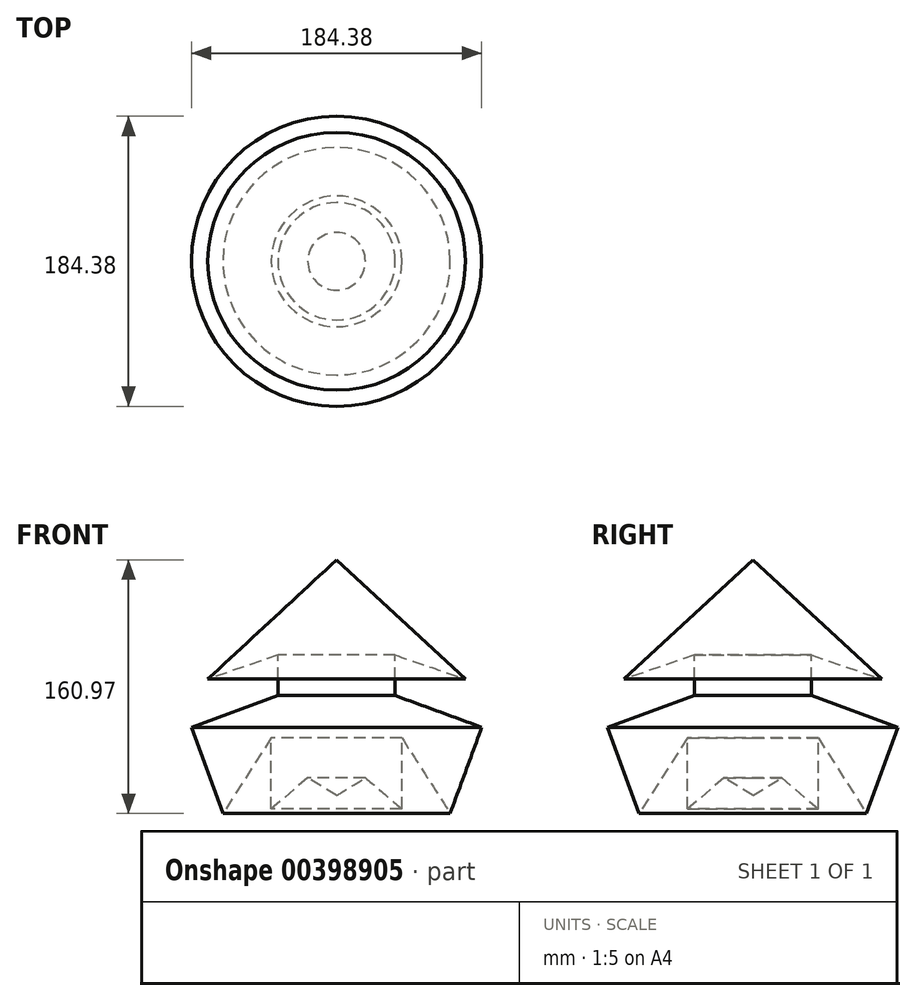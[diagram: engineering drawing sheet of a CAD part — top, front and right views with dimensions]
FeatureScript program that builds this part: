
annotation { "Feature Type Name" : "Feature", "Feature Type Description" : "" }
export const myFeature = defineFeature(function(context is Context, id is Id, definition is map)
    precondition{}
    {
        {
            var Q0;
            Q0=qCreatedBy(makeId("Right.planeOp"),FACE);
            var sketch = newSketch(context, id + "F0", { "sketchPlane" : qUnion([Q0])});
            skLineSegment(sketch, "E0", {"start": v(0, 75.7) * mm, "end": v(0, -73.9) * mm});
            skLineSegment(sketch, "E1", {"start": v(0, 75.7) * mm, "end": v(81.81, 0) * mm});
            skLineSegment(sketch, "E2", {"start": v(81.81, 0) * mm, "end": v(37.24, 15.22) * mm});
            skLineSegment(sketch, "E3", {"start": v(37.24, 15.22) * mm, "end": v(37.24, -10.5) * mm});
            skLineSegment(sketch, "E4", {"start": v(37.24, -10.5) * mm, "end": v(92.2, -30.59) * mm});
            skLineSegment(sketch, "E5", {"start": v(92.2, -30.59) * mm, "end": v(71.12, -88.2) * mm});
            skLineSegment(sketch, "E6", {"start": v(72.19, -85.28) * mm, "end": v(41.52, -37.33) * mm});
            skLineSegment(sketch, "E7", {"start": v(41.52, -37.33) * mm, "end": v(41.52, -82.44) * mm});
            skLineSegment(sketch, "E8", {"start": v(41.52, -82.44) * mm, "end": v(18.32, -62.74) * mm});
            skLineSegment(sketch, "E9", {"start": v(18.32, -62.74) * mm, "end": v(0, -73.9) * mm});
            skSolve(sketch);
        }
        {
            var Q0;
            Q0=makeQuery(id+"F0.imprint","IMPRINT",FACE,{"disambiguationData":[TD([[makeQuery(id+"F0.imprint","IMPRINT",EDGE,{"derivedFrom":sQuery(id+"F0.wireOp",EDGE,"E0")}),1.0]])]});
            var Q1;
            Q1=sQuery(id+"F0.wireOp",EDGE,"E0");
            revolve(context, id + "F1", {"entities" : qUnion([Q0]), "axis" : qUnion([Q1]), "revolveType" : RevolveType.FULL});
        }
    });
